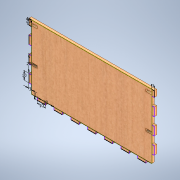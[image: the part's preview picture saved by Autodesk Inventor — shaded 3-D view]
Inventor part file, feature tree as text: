
AUTODESK INVENTOR PART (.ipt)
format: ipt  version: 2021 (Build 250183000, 183)  size: 221,184 bytes
history: native  units: mm
features: extrude x3, sketch x3
ambient origin geometry x8: Origin, YZ Plane, XZ Plane, XY Plane, X Axis, Y Axis, Z Axis, Center Point
bodies: Solid1 (feature_tree)
feature tree (6):
  extrude  "Extrusion1"  Depth=77.0mm
  extrude  "Extrusion2"  Depth=3.0mm
  extrude  "Extrusion3"  Depth=70.0mm
  sketch  "Sketch1"  dims[d0=144.0mm d1=77.0mm]
  sketch  "Sketch2"  dims[d2=3.0mm d3=0.0mm d4=3.0mm]
  sketch  "Sketch3"  dims[d5=10.0mm d6=70.0mm d8=20.0mm d9=10.0mm d11=10.0mm d13=3.0mm d14=10.0mm d15=30.0mm d17=20.0mm d18=10.0mm d20=10.0mm d22=3.0mm d23=7.0mm d24=3.0mm d25=3.0mm d26=0.0mm d27=7.0mm d28=3.0mm d29=20.0mm d31=137.0mm d32=20.0mm d34=41.0mm d37=0.0mm d38=0.0mm]
